# Revit family: IS_CerafineO_BC747_BIM_GB
name_source: partatom
category: Plumbing Fixtures
revit_build: Autodesk Revit 2017 (Build: 20160225_1515(x64)
units: mm (PartAtom-declared; Revit-internal decimal feet)

## family parameters
Always vertical = No
Cut with Voids When Loaded = No
OmniClass Number = 23.45.55.00
OmniClass Title = Sanitary Faucets, Wastes
Part Type = Normal
Room Calculation Point = No
Round Connector Dimension = Use Diameter
Shared = No
Work Plane-Based = No

## types (1)
- BC747U4 - CERAFINE O SHR KIT SYS MBLK/CHR HD/200
    Accessories = https://www.idealspec.co.uk
    AreaUnits = millimeters
    AssetType = Fixed
    BIMObjectName = ISI_IdealStandard_Shower mixers_CerafineO_BC747
    BIMobject category = Taps & Mixers
    BIMobject category code = sanitary-taps-mixers
    BIMobject main category = Sanitary
    BIMobject main category code = sanitary
    BarCode = 3800861083009
    Brand = Ideal Standard
    Brand url = http://www.idealstandard.co.uk
    Color = Matt Black
    ConnectionType = Plumbing
    CurrencyUnit = £
    CurrentRevision = 1
    Date of publishing = 09/09/2020
    Description = CERAFINE O Shower Kit SYS MBLK/CHR HD/200
    DurationUnit = Year
    Edition number = 1
    ExpectedLife = 30
    FaucetFunction = MIXED
    FaucetOperation = OTHER
    FaucetType = OTHER
    Features = Shower Kit SYS MBLK/CHR HD/200
    Finish = Matt Black
    GTIN code = https://3800861083009
    Help = https://www.idealspec.co.uk
    IFC Classification = Sanitary Terminal
    IfcExportAs = IfcValveType
    IfcExportType = FAUCET
    Installation instructions = https://www.idealspec.co.uk
    InstallationInstructions = https://www.idealspec.co.uk
    IsHighPressure = No
    LinearUnits = millimeters
    MainColor = Matt Black
    MaintenanceInformation = https://www.idealspec.co.uk
    Manufacturer = Ideal Standard
    Manufacturer name = Ideal Standard
    ManufacturerURL = https://www.idealspec.co.uk
    Material = Brass
    Material main = Brass
    MaterialThickness = 0 mm  [stored 0 ft]
    Model = BC747U4
    ModelNumber = BC747U4
    ModelReference = CERAFINE O Shower Kit SYS MBLK/CHR HD/200
    NBS Reference Code = 45-35-70/335
    NBS Reference Description = Shower mixers
    Name = Shower mixers_CerafineO_BC747_IdealStandard
    NettWeight = 4,04 KG
    NominalDepth = 481 mm
    NominalHeight = 1194 mm
    NominalLength = 481 mm
    NominalWidth = 293 mm
    OmniClass Code = 23.45.55.00
    OmniClass Description = Sanitary Faucets, Wastes
    Product Guid = 99ea1c98-67ac-4861-855b-908c4a8a1cf3
    Product SKU = BC747
    Product certification = https://www.idealspec.co.uk
    Product data url = https://bimobject.com
    Product family = CERAFINE MODEL O
    Product group = SHOWER SYSTEM
    Product name = A_CERAFINE O SHR KIT SYS MBLK/CHR HD/200
    Product url = https://www.idealspec.co.uk
    ProductInformation = https://www.idealspec.co.uk
    QR code = http://bimobject.com
    Shape = Sculptured
    Size = 293 x 481 x 1194 mm
    Space = Internal
    SpareParts = https://fastpart-spares.co.uk
    Technical description = https://www.idealspec.co.uk
    TestPressure = 10 bar
    UNSPSC Code = 30181700
    URL = https://www.idealspec.co.uk
    Uniclass 1.4 Code = L725111
    Uniclass 1.4 Description = Mixer taps
    Uniclass 2.0 Code = Pr_40_30_96_81
    Uniclass 2.0 Description = Shower Thermostatic Water Supply Sets
    Uniclass 2015 Code = Pr_40_20_87_78
    Uniclass 2015 Name = Shower manual water supply sets
    Uniclass2015Code = Pr_40_20_87_78
    Uniclass2015Title = Shower manual water supply sets
    Uniclass2015Version = v1.1
    ValveMechanism = Thermostatic
    ValveOperation = Lever
    Version = 1
    VolumeUnits = Litres
    WRASURL = https://www.wras.co.uk
    WarrantyDescription = Manufacturers Warranty
    WarrantyDurationParts = 5
    WarrantyDurationUnit = Year
    WarrantyGuarantorParts = https://www.idealspec.co.uk

note: [stored X ft] marks values corroborated as IEEE doubles in the binary element streams (Revit-internal decimal feet)

## geometry (parser evidence)
native form markers: Sweep x2
no freeform markers — native parametric forms only
